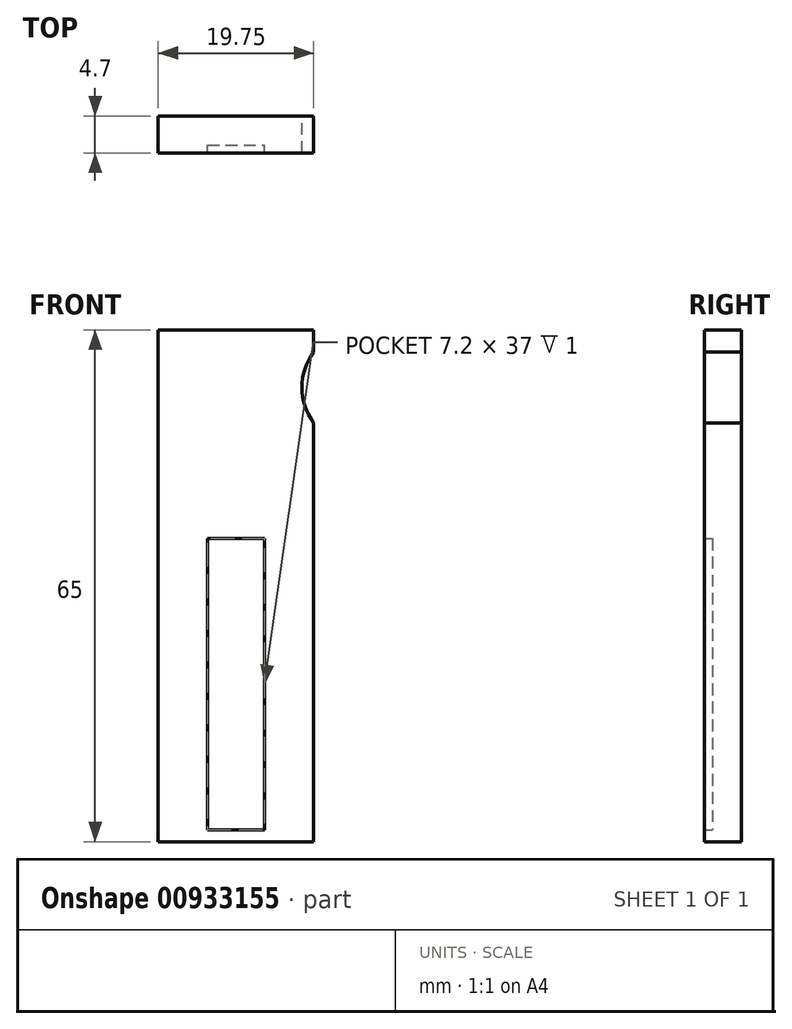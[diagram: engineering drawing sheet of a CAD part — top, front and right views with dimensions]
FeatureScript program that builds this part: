
annotation { "Feature Type Name" : "Feature", "Feature Type Description" : "" }
export const myFeature = defineFeature(function(context is Context, id is Id, definition is map)
    precondition{}
    {
        {
            var Q0;
            Q0=qCreatedBy(makeId("Front.planeOp"),FACE);
            var sketch = newSketch(context, id + "F0", { "sketchPlane" : qUnion([Q0])});
            skLineSegment(sketch, "E0.bottom", {"start": v(0, 0) * mm, "end": v(19.75, 0) * mm});
            skLineSegment(sketch, "E0.top", {"start": v(0, 65) * mm, "end": v(19.75, 65) * mm});
            skLineSegment(sketch, "E0.left", {"start": v(0, 0) * mm, "end": v(0, 65) * mm});
            skLineSegment(sketch, "E0.right", {"start": v(19.75, 0) * mm, "end": v(19.75, 65) * mm});
            skLineSegment(sketch, "E1", {"start": v(9.87, 65) * mm, "end": v(9.87, 0) * mm, "construction": true});
            skLineSegment(sketch, "E2.bottom", {"start": v(6.27, 38.5) * mm, "end": v(13.47, 38.5) * mm});
            skLineSegment(sketch, "E2.top", {"start": v(6.27, 1.5) * mm, "end": v(13.47, 1.5) * mm});
            skLineSegment(sketch, "E2.left", {"start": v(6.27, 38.5) * mm, "end": v(6.27, 1.5) * mm});
            skLineSegment(sketch, "E2.right", {"start": v(13.47, 38.5) * mm, "end": v(13.47, 1.5) * mm});
            skPoint(sketch, "E3", {"position": v(9.87, 38.5) * mm});
            skSolve(sketch);
        }
        {
            var Q0;
            Q0=makeQuery(id+"F0.imprint","IMPRINT",FACE,{"disambiguationData":[TD([[makeQuery(id+"F0.imprint","IMPRINT",EDGE,{"derivedFrom":sQuery(id+"F0.wireOp",EDGE,"E0.bottom")}),1.0]])]});
            extrude(context, id + "F1", {"entities" : qUnion([Q0]), "depth" : 4.7 * mm, "offsetDistance" : 25 * mm});
        }
        {
            var Q0;
            Q0=makeQuery(id+"F0.imprint","IMPRINT",FACE,{"disambiguationData":[TD([[makeQuery(id+"F0.imprint","IMPRINT",EDGE,{"derivedFrom":sQuery(id+"F0.wireOp",EDGE,"E2.bottom")}),-1.0]])]});
            extrude(context, id + "F2", {"entities" : qUnion([Q0]), "operationType" : NewBodyOperationType.ADD, "depth" : 3.7 * mm, "offsetDistance" : 25 * mm});
        }
        {
            var Q0;
            {var subQ0=sQuery(id+"F0.wireOp",EDGE,"E2.right");var subQ1=sQuery(id+"F0.wireOp",EDGE,"E2.left");var subQ2=sQuery(id+"F0.wireOp",EDGE,"E2.top");var subQ3=sQuery(id+"F0.wireOp",EDGE,"E2.bottom");Q0=makeQuery(id+"F2.boolean.opBoolean","MERGE",FACE,{"derivedFrom":[makeQuery(id+"F1.opExtrude","CAP_FACE",FACE,{"disambiguationData":[OSD([sQuery(id+"F0.wireOp",EDGE,"E0.bottom"),sQuery(id+"F0.wireOp",EDGE,"E0.top"),sQuery(id+"F0.wireOp",EDGE,"E0.left"),sQuery(id+"F0.wireOp",EDGE,"E0.right"),subQ3,subQ2,subQ1,subQ0])],"isStart":true}),makeQuery(id+"F2.opExtrude","CAP_FACE",FACE,{"disambiguationData":[OSD([subQ3,subQ2,subQ1,subQ0])],"isStart":true})]});}
            var sketch = newSketch(context, id + "F3", { "sketchPlane" : qUnion([Q0])});
            skCircle(sketch, "E4", {"center": v(-25.76, 57.7) * mm, "radius": 7.5 * mm});
            skLineSegment(sketch, "E5", {"start": v(-9.87, 65) * mm, "end": v(-9.87, 0) * mm, "construction": true});
            skCircle(sketch, "E6.MirrorC", {"center": v(6, 57.7) * mm, "radius": 7.5 * mm});
            skSolve(sketch);
        }
        {
            var Q0;
            {var subQ0=sQuery(id+"F3.wireOp",EDGE,"E4");var subQ1=makeQuery(id+"F1.opExtrude","CAP_EDGE",EDGE,{"disambiguationData":[OSD([sQuery(id+"F0.wireOp",EDGE,"E0.right")])],"isStart":true});var subQ2=makeQuery(id+"F3.imprint","INTERSECT",VERTEX,{"disambiguationData":[OD(0.0)],"derivedFrom":[subQ1,subQ0]});Q0=makeQuery(id+"F3.imprint","IMPRINT",FACE,{"disambiguationData":[TD([[makeQuery(id+"F3.imprint","IMPRINT",EDGE,{"disambiguationData":[TD([[subQ2,-1.0]])],"derivedFrom":subQ0}),1.0]])]});}
            var Q1;
            {var subQ0=sQuery(id+"F3.wireOp",EDGE,"E6.MirrorC");var subQ1=makeQuery(id+"F1.opExtrude","CAP_EDGE",EDGE,{"disambiguationData":[OSD([sQuery(id+"F0.wireOp",EDGE,"E0.left")])],"isStart":true});var subQ2=makeQuery(id+"F3.imprint","INTERSECT",VERTEX,{"disambiguationData":[OD(0.0)],"derivedFrom":[subQ1,subQ0]});Q1=makeQuery(id+"F3.imprint","IMPRINT",FACE,{"disambiguationData":[TD([[makeQuery(id+"F3.imprint","IMPRINT",EDGE,{"disambiguationData":[TD([[subQ2,-1.0]])],"derivedFrom":subQ0}),-1.0]])]});}
            extrude(context, id + "F4", {"entities" : qUnion([Q0, Q1]), "operationType" : NewBodyOperationType.REMOVE, "endBound" : BoundingType.THROUGH_ALL, "oppositeDirection" : true, "depth" : 25 * mm, "offsetDistance" : 25 * mm});
        }
    });
